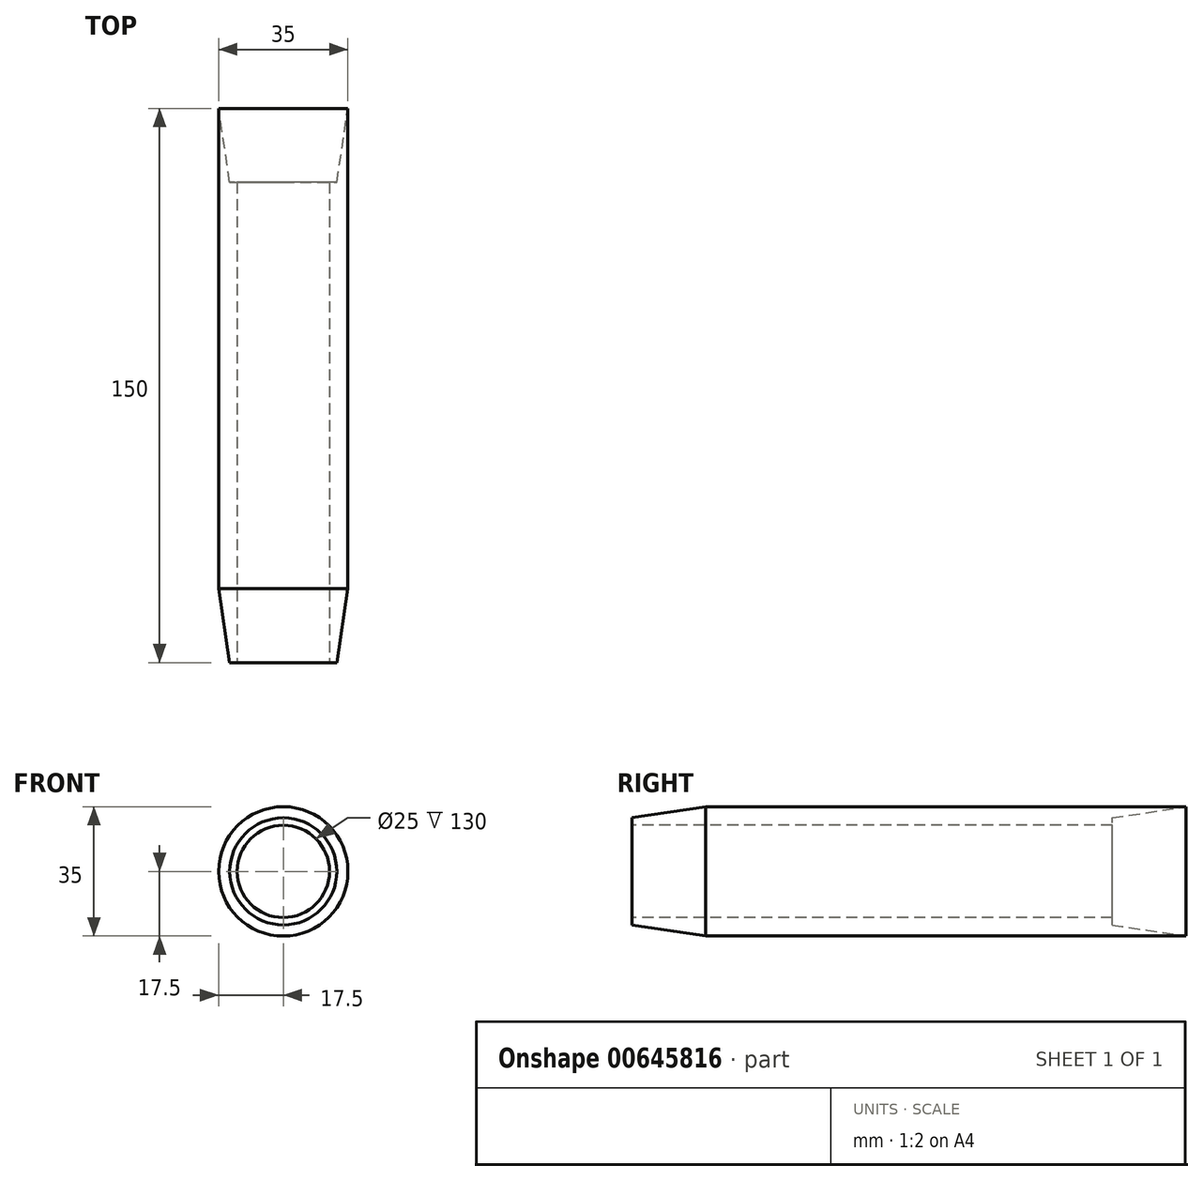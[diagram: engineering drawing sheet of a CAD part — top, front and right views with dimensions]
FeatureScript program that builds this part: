
annotation { "Feature Type Name" : "Feature", "Feature Type Description" : "" }
export const myFeature = defineFeature(function(context is Context, id is Id, definition is map)
    precondition{}
    {
        {
            var Q0;
            Q0=qCreatedBy(makeId("Top.planeOp"),FACE);
            var sketch = newSketch(context, id + "F0", { "sketchPlane" : qUnion([Q0])});
            skLineSegment(sketch, "E0", {"start": v(0, 0) * mm, "end": v(0, 150) * mm, "construction": true});
            skLineSegment(sketch, "E1", {"start": v(17.5, 0) * mm, "end": v(17.5, 150) * mm, "construction": true});
            skLineSegment(sketch, "E2", {"start": v(-61.8, 150) * mm, "end": v(89.31, 150) * mm, "construction": true});
            skLineSegment(sketch, "E3", {"start": v(12.5, 0) * mm, "end": v(12.5, 150) * mm, "construction": true});
            skLineSegment(sketch, "E4", {"start": v(-32.67, 20) * mm, "end": v(48.75, 20) * mm, "construction": true});
            skLineSegment(sketch, "E5", {"start": v(12.5, 0) * mm, "end": v(14.5, 0) * mm});
            skPoint(sketch, "E6", {"position": v(17.5, 20) * mm});
            skLineSegment(sketch, "E7", {"start": v(14.5, 0) * mm, "end": v(17.5, 20) * mm});
            skLineSegment(sketch, "E8", {"start": v(17.5, 150) * mm, "end": v(17.5, 20) * mm});
            skPoint(sketch, "E9", {"position": v(12.5, 130) * mm});
            skLineSegment(sketch, "E10", {"start": v(14.5, 130) * mm, "end": v(12.5, 130) * mm});
            skLineSegment(sketch, "E11", {"start": v(14.5, 130) * mm, "end": v(17.5, 150) * mm});
            skLineSegment(sketch, "E12", {"start": v(12.5, 0) * mm, "end": v(12.5, 130) * mm});
            skSolve(sketch);
        }
        {
            var Q0;
            Q0=makeQuery(id+"F0.imprint","IMPRINT",FACE,{"disambiguationData":[TD([[makeQuery(id+"F0.imprint","IMPRINT",EDGE,{"derivedFrom":sQuery(id+"F0.wireOp",EDGE,"E5")}),1.0]])]});
            var Q1;
            Q1=sQuery(id+"F0.wireOp",EDGE,"E0");
            revolve(context, id + "F1", {"entities" : qUnion([Q0]), "axis" : qUnion([Q1]), "revolveType" : RevolveType.FULL});
        }
    });
